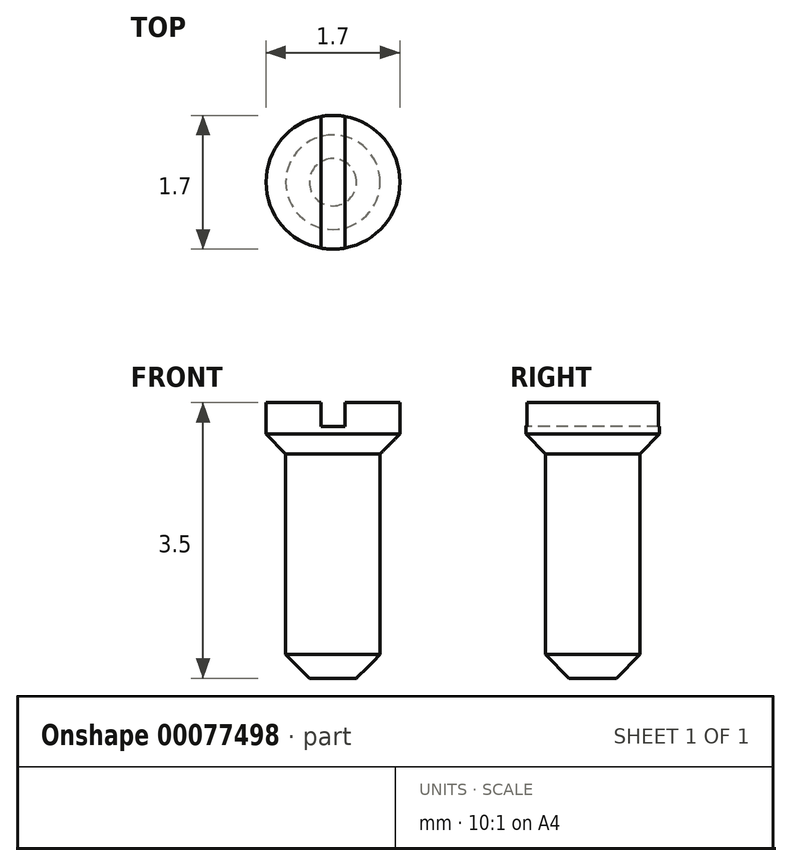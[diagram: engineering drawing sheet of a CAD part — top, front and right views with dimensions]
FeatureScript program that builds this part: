
annotation { "Feature Type Name" : "Feature", "Feature Type Description" : "" }
export const myFeature = defineFeature(function(context is Context, id is Id, definition is map)
    precondition{}
    {
        {
            var Q0;
            Q0=qCreatedBy(makeId("Front.planeOp"),FACE);
            var sketch = newSketch(context, id + "F0", { "sketchPlane" : qUnion([Q0])});
            skLineSegment(sketch, "E0", {"start": v(0, 0) * mm, "end": v(0.3, 0) * mm});
            skLineSegment(sketch, "E1", {"start": v(0.3, 0) * mm, "end": v(0.6, 0.3) * mm});
            skLineSegment(sketch, "E2", {"start": v(0.6, 0.3) * mm, "end": v(0.6, 2.85) * mm});
            skLineSegment(sketch, "E3", {"start": v(0.6, 2.85) * mm, "end": v(0.85, 3.1) * mm});
            skLineSegment(sketch, "E4", {"start": v(0.85, 3.1) * mm, "end": v(0.85, 3.5) * mm});
            skLineSegment(sketch, "E5", {"start": v(0.85, 3.5) * mm, "end": v(0, 3.5) * mm});
            skLineSegment(sketch, "E6", {"start": v(0, 3.5) * mm, "end": v(0, 0) * mm});
            skSolve(sketch);
        }
        {
            var Q0;
            Q0=makeQuery(id+"F0.imprint","IMPRINT",FACE,{"disambiguationData":[TD([[makeQuery(id+"F0.imprint","IMPRINT",EDGE,{"derivedFrom":sQuery(id+"F0.wireOp",EDGE,"E0")}),1.0]])]});
            var Q1;
            Q1=sQuery(id+"F0.wireOp",EDGE,"E6");
            revolve(context, id + "F1", {"entities" : qUnion([Q0]), "axis" : qUnion([Q1]), "revolveType" : RevolveType.FULL});
        }
        {
            var Q0;
            Q0=makeQuery(id+"F1.opRevolve","SWEPT_FACE",FACE,{"disambiguationData":[OSD([sQuery(id+"F0.wireOp",EDGE,"E5")])]});
            var sketch = newSketch(context, id + "F2", { "sketchPlane" : qUnion([Q0])});
            skLineSegment(sketch, "E7", {"start": v(-0.15, 0.84) * mm, "end": v(-0.15, -0.84) * mm});
            skLineSegment(sketch, "E8", {"start": v(0.15, -0.84) * mm, "end": v(0.15, 0.84) * mm});
            skSolve(sketch);
        }
        {
            var Q0;
            {var subQ2=sQuery(id+"F2.wireOp",EDGE,"E7");Q0=makeQuery(id+"F2.imprint","IMPRINT",FACE,{"disambiguationData":[TD([[makeQuery(id+"F2.imprint","IMPRINT",EDGE,{"derivedFrom":subQ2}),1.0]])]});}
            extrude(context, id + "F3", {"entities" : qUnion([Q0]), "operationType" : NewBodyOperationType.REMOVE, "oppositeDirection" : true, "depth" : 0.3 * mm});
        }
    });
